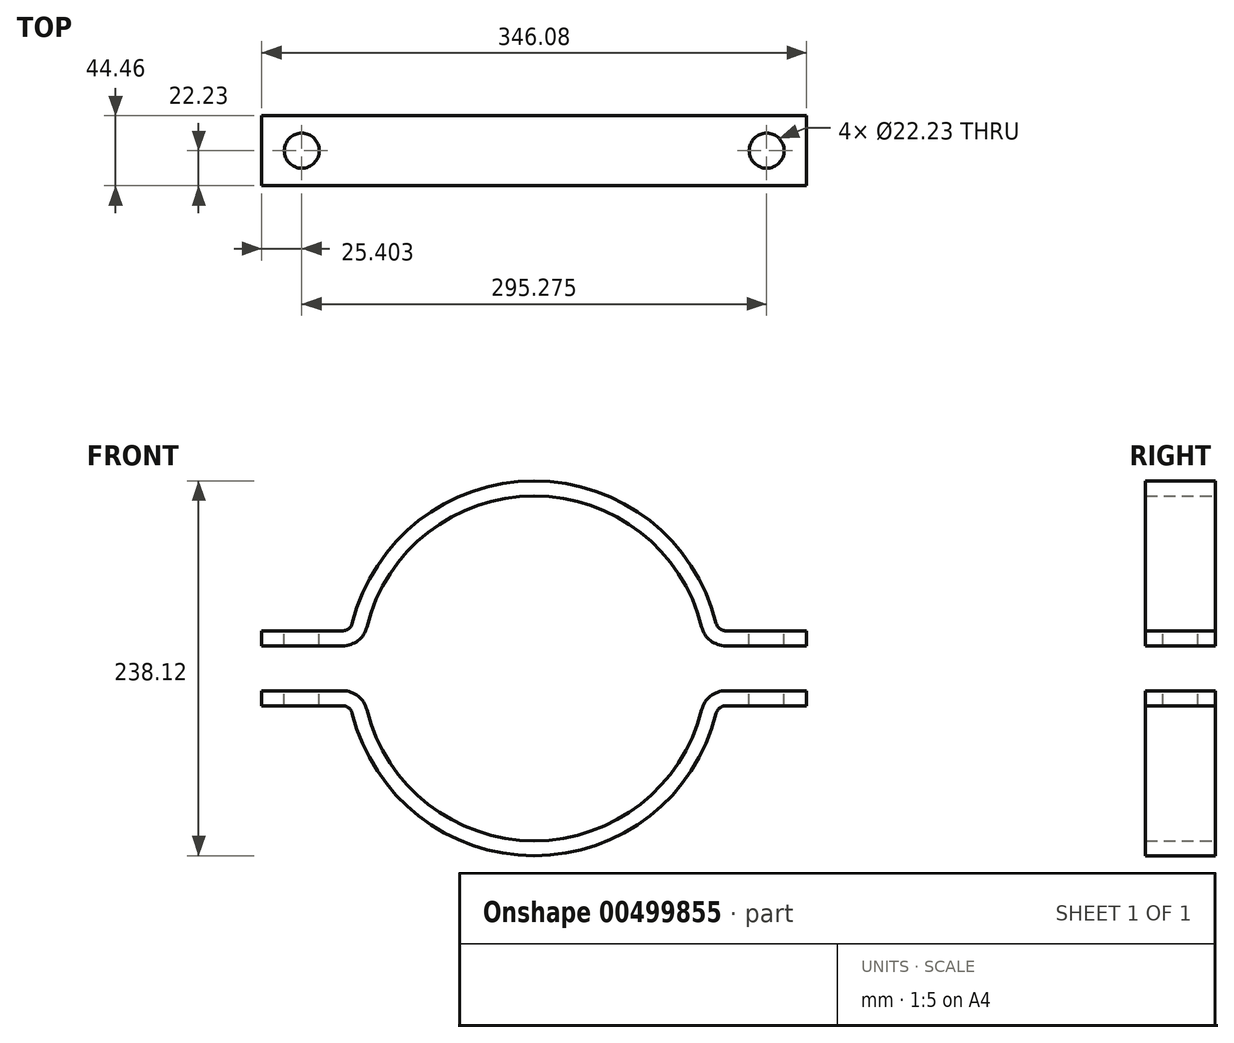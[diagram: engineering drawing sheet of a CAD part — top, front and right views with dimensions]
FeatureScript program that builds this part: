
annotation { "Feature Type Name" : "Feature", "Feature Type Description" : "" }
export const myFeature = defineFeature(function(context is Context, id is Id, definition is map)
    precondition{}
    {
        {
            var Q0;
            Q0=qCreatedBy(makeId("Front.planeOp"),FACE);
            var sketch = newSketch(context, id + "F0", { "sketchPlane" : qUnion([Q0])});
            skArc(sketch, "E0", {"start": v(108.6, 14.29) * mm, "mid": v(0, 109.54) * mm, "end": v(-108.6, 14.29) * mm});
            skArc(sketch, "E1", {"start": v(116.66, 23.81) * mm, "mid": v(0, 119.06) * mm, "end": v(-116.66, 23.81) * mm});
            skLineSegment(sketch, "E2.bottom", {"start": v(173.04, 14.29) * mm, "end": v(108.6, 14.29) * mm});
            skLineSegment(sketch, "E2.top", {"start": v(173.04, 23.81) * mm, "end": v(116.66, 23.81) * mm});
            skLineSegment(sketch, "E2.left", {"start": v(173.04, 14.29) * mm, "end": v(173.04, 23.81) * mm});
            skLineSegment(sketch, "E2.right", {"start": v(-173.04, 14.29) * mm, "end": v(-173.04, 23.81) * mm});
            skPoint(sketch, "E2.middle", {"position": v(0, 19.05) * mm});
            skLineSegment(sketch, "E3.trimOffspring", {"start": v(-108.6, 14.29) * mm, "end": v(-173.04, 14.29) * mm});
            skLineSegment(sketch, "E4.trimOffspring", {"start": v(-116.66, 23.81) * mm, "end": v(-173.04, 23.81) * mm});
            skLineSegment(sketch, "E5.MirrorCS", {"start": v(-108.6, -14.29) * mm, "end": v(-173.04, -14.29) * mm});
            skLineSegment(sketch, "E6.MirrorCS", {"start": v(-116.66, -23.81) * mm, "end": v(-173.04, -23.81) * mm});
            skLineSegment(sketch, "E7.MirrorCS", {"start": v(-173.04, -14.29) * mm, "end": v(-173.04, -23.81) * mm});
            skArc(sketch, "E8.MirrorCS", {"start": v(108.6, -14.29) * mm, "mid": v(0, -109.54) * mm, "end": v(-108.6, -14.29) * mm});
            skArc(sketch, "E9.MirrorCS", {"start": v(116.66, -23.81) * mm, "mid": v(0, -119.06) * mm, "end": v(-116.66, -23.81) * mm});
            skLineSegment(sketch, "E10.MirrorCS", {"start": v(173.04, -14.29) * mm, "end": v(108.6, -14.29) * mm});
            skLineSegment(sketch, "E11.MirrorCS", {"start": v(173.04, -23.81) * mm, "end": v(116.66, -23.81) * mm});
            skLineSegment(sketch, "E12.MirrorCS", {"start": v(173.04, -14.29) * mm, "end": v(173.04, -23.81) * mm});
            skSolve(sketch);
        }
        {
            var Q0;
            Q0=makeQuery(id+"F0.imprint","IMPRINT",FACE,{"disambiguationData":[TD([[makeQuery(id+"F0.imprint","IMPRINT",EDGE,{"derivedFrom":sQuery(id+"F0.wireOp",EDGE,"E0")}),-1.0]])]});
            var Q1;
            Q1=makeQuery(id+"F0.imprint","IMPRINT",FACE,{"disambiguationData":[TD([[makeQuery(id+"F0.imprint","IMPRINT",EDGE,{"derivedFrom":sQuery(id+"F0.wireOp",EDGE,"E5.MirrorCS")}),1.0]])]});
            extrude(context, id + "F1", {"entities" : qUnion([Q0, Q1]), "endBound" : BoundingType.SYMMETRIC, "depth" : 44.45 * mm});
        }
        {
            var Q0;
            Q0=makeQuery(id+"F1.opExtrude","SWEPT_EDGE",EDGE,{"disambiguationData":[OSD([sQuery(id+"F0.wireOp",EDGE,"E1"),sQuery(id+"F0.wireOp",EDGE,"E4.trimOffspring")])]});
            var Q1;
            Q1=makeQuery(id+"F1.opExtrude","SWEPT_EDGE",EDGE,{"disambiguationData":[OSD([sQuery(id+"F0.wireOp",EDGE,"E1"),sQuery(id+"F0.wireOp",EDGE,"E2.top")])]});
            var Q2;
            Q2=makeQuery(id+"F1.opExtrude","SWEPT_EDGE",EDGE,{"disambiguationData":[OSD([sQuery(id+"F0.wireOp",EDGE,"E9.MirrorCS"),sQuery(id+"F0.wireOp",EDGE,"E11.MirrorCS")])]});
            var Q3;
            Q3=makeQuery(id+"F1.opExtrude","SWEPT_EDGE",EDGE,{"disambiguationData":[OSD([sQuery(id+"F0.wireOp",EDGE,"E6.MirrorCS"),sQuery(id+"F0.wireOp",EDGE,"E9.MirrorCS")])]});
            fillet(context, id + "F2", {"entities" : qUnion([Q0, Q1, Q2, Q3]), "radius" : 6.35 * mm, "tangentPropagation" : true, "allowEdgeOverflow" : false});
        }
        {
            var Q0;
            Q0=makeQuery(id+"F1.opExtrude","SWEPT_EDGE",EDGE,{"disambiguationData":[OSD([sQuery(id+"F0.wireOp",EDGE,"E0"),sQuery(id+"F0.wireOp",EDGE,"E2.bottom")])]});
            var Q1;
            Q1=makeQuery(id+"F1.opExtrude","SWEPT_EDGE",EDGE,{"disambiguationData":[OSD([sQuery(id+"F0.wireOp",EDGE,"E8.MirrorCS"),sQuery(id+"F0.wireOp",EDGE,"E10.MirrorCS")])]});
            var Q2;
            Q2=makeQuery(id+"F1.opExtrude","SWEPT_EDGE",EDGE,{"disambiguationData":[OSD([sQuery(id+"F0.wireOp",EDGE,"E5.MirrorCS"),sQuery(id+"F0.wireOp",EDGE,"E8.MirrorCS")])]});
            var Q3;
            Q3=makeQuery(id+"F1.opExtrude","SWEPT_EDGE",EDGE,{"disambiguationData":[OSD([sQuery(id+"F0.wireOp",EDGE,"E0"),sQuery(id+"F0.wireOp",EDGE,"E3.trimOffspring")])]});
            fillet(context, id + "F3", {"entities" : qUnion([Q0, Q1, Q2, Q3]), "radius" : 15.88 * mm, "tangentPropagation" : true, "allowEdgeOverflow" : false});
        }
        {
            var Q0;
            Q0=makeQuery(id+"F1.opExtrude","SWEPT_FACE",FACE,{"disambiguationData":[OSD([sQuery(id+"F0.wireOp",EDGE,"E2.top")])]});
            var sketch = newSketch(context, id + "F4", { "sketchPlane" : qUnion([Q0])});
            skCircle(sketch, "E13", {"center": v(-147.64, 0) * mm, "radius": 11.11 * mm});
            skCircle(sketch, "E14.MirrorC", {"center": v(147.64, 0) * mm, "radius": 11.11 * mm});
            skSolve(sketch);
        }
        {
            var Q0;
            Q0 = qSketchRegion(id + "F4", true);
            extrude(context, id + "F5", {"entities" : qUnion([Q0]), "operationType" : NewBodyOperationType.REMOVE, "endBound" : BoundingType.THROUGH_ALL, "oppositeDirection" : true, "depth" : 101.6 * mm});
        }
    });
